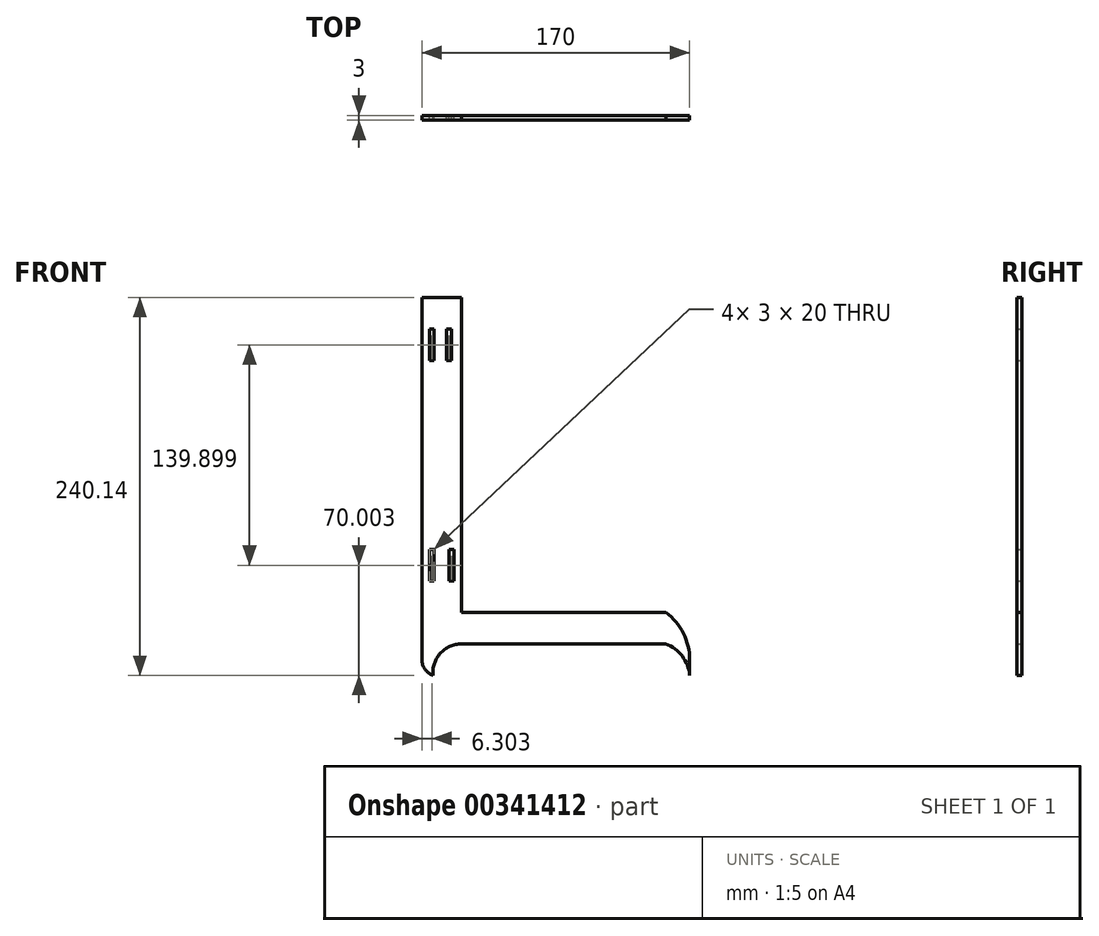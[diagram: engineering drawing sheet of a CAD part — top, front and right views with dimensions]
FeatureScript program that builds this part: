
annotation { "Feature Type Name" : "Feature", "Feature Type Description" : "" }
export const myFeature = defineFeature(function(context is Context, id is Id, definition is map)
    precondition{}
    {
        {
            var Q0;
            Q0=qCreatedBy(makeId("Front.planeOp"),FACE);
            var sketch = newSketch(context, id + "F0", { "sketchPlane" : qUnion([Q0])});
            skLineSegment(sketch, "E0.top", {"start": v(12.5, 100.07) * mm, "end": v(-12.5, 100.07) * mm});
            skLineSegment(sketch, "E0.left", {"start": v(12.5, -100.07) * mm, "end": v(12.5, 100.07) * mm});
            skLineSegment(sketch, "E0.right", {"start": v(-12.5, -100.07) * mm, "end": v(-12.5, 100.07) * mm});
            skPoint(sketch, "E0.middle", {"position": v(0, 0) * mm});
            skPoint(sketch, "E1.endSnap0", {"position": v(0, 100.07) * mm});
            skLineSegment(sketch, "E2.top", {"start": v(-6.23, 59.83) * mm, "end": v(-4.69, 59.83) * mm});
            skLineSegment(sketch, "E2.right", {"start": v(-4.69, 79.83) * mm, "end": v(-4.69, 59.83) * mm});
            skLineSegment(sketch, "E3.top", {"start": v(-6.25, 59.83) * mm, "end": v(-7.69, 59.83) * mm});
            skLineSegment(sketch, "E3.right", {"start": v(-7.69, 79.83) * mm, "end": v(-7.69, 59.83) * mm});
            skLineSegment(sketch, "E4", {"start": v(-7.69, 59.83) * mm, "end": v(-4.69, 59.83) * mm});
            skLineSegment(sketch, "E5", {"start": v(3.13, 79.83) * mm, "end": v(3.13, 59.83) * mm});
            skLineSegment(sketch, "E6", {"start": v(3.13, 59.83) * mm, "end": v(6.13, 59.83) * mm});
            skLineSegment(sketch, "E7", {"start": v(6.13, 79.83) * mm, "end": v(6.13, 59.83) * mm});
            skLineSegment(sketch, "E8", {"start": v(-7.69, 79.83) * mm, "end": v(-4.69, 79.83) * mm});
            skLineSegment(sketch, "E9", {"start": v(3.13, 79.83) * mm, "end": v(6.13, 79.83) * mm});
            skLineSegment(sketch, "E10", {"start": v(-12.5, -80.07) * mm, "end": v(-12.5, -100.07) * mm});
            skLineSegment(sketch, "E11", {"start": v(-4.69, -80.07) * mm, "end": v(-7.69, -80.07) * mm});
            skLineSegment(sketch, "E12", {"start": v(-7.69, -80.07) * mm, "end": v(-7.69, -60.07) * mm});
            skLineSegment(sketch, "E13", {"start": v(-7.69, -60.07) * mm, "end": v(-4.69, -60.07) * mm});
            skLineSegment(sketch, "E14", {"start": v(-4.69, -60.07) * mm, "end": v(-4.69, -80.07) * mm});
            skLineSegment(sketch, "E15", {"start": v(6.25, -60.07) * mm, "end": v(7.8, -60.07) * mm});
            skLineSegment(sketch, "E16", {"start": v(7.8, -60.07) * mm, "end": v(4.8, -60.07) * mm});
            skLineSegment(sketch, "E17", {"start": v(7.8, -80.07) * mm, "end": v(7.8, -60.07) * mm});
            skLineSegment(sketch, "E18", {"start": v(4.8, -60.07) * mm, "end": v(4.8, -80.07) * mm});
            skLineSegment(sketch, "E19", {"start": v(4.8, -80.07) * mm, "end": v(7.8, -80.07) * mm});
            skLineSegment(sketch, "E20.right", {"start": v(-12.5, -100.07) * mm, "end": v(-12.5, -130.07) * mm});
            skLineSegment(sketch, "E21.bottom", {"start": v(12.5, -130.07) * mm, "end": v(12.5, -130.07) * mm});
            skLineSegment(sketch, "E21.top", {"start": v(12.5, -100.07) * mm, "end": v(12.5, -100.07) * mm});
            skLineSegment(sketch, "E22.right", {"start": v(157.5, -130.07) * mm, "end": v(157.5, -130.07) * mm});
            skArc(sketch, "E23", {"start": v(157.5, -130.07) * mm, "mid": v(153.55, -113.3) * mm, "end": v(142.5, -100.07) * mm});
            skLineSegment(sketch, "E24", {"start": v(12.5, -100.07) * mm, "end": v(142.5, -100.07) * mm});
            skArc(sketch, "E25", {"start": v(-12.5, -130.07) * mm, "mid": v(-10.55, -136.19) * mm, "end": v(-5.44, -140.07) * mm});
            skLineSegment(sketch, "E26.top", {"start": v(-12.5, 100.07) * mm, "end": v(12.5, 100.07) * mm});
            skLineSegment(sketch, "E27", {"start": v(12.5, -120.07) * mm, "end": v(142.3, -120.07) * mm});
            skArc(sketch, "E28", {"start": v(12.5, -120.07) * mm, "mid": v(-0.93, -126.06) * mm, "end": v(-5.44, -140.07) * mm});
            skLineSegment(sketch, "E29", {"start": v(12.5, -120.07) * mm, "end": v(20.48, -120.07) * mm});
            skLineSegment(sketch, "E30", {"start": v(20.48, -120.07) * mm, "end": v(12.5, -120.07) * mm});
            skArc(sketch, "E31", {"start": v(157.5, -140.07) * mm, "mid": v(152.8, -127.85) * mm, "end": v(142.3, -120.07) * mm});
            skLineSegment(sketch, "E32", {"start": v(157.5, -130.07) * mm, "end": v(157.5, -140.07) * mm});
            skSolve(sketch);
        }
        {
            var Q0;
            Q0 = qSketchRegion(id + "F0", true);
            extrude(context, id + "F1", {"entities" : qUnion([Q0]), "depth" : 3 * mm});
        }
    });
